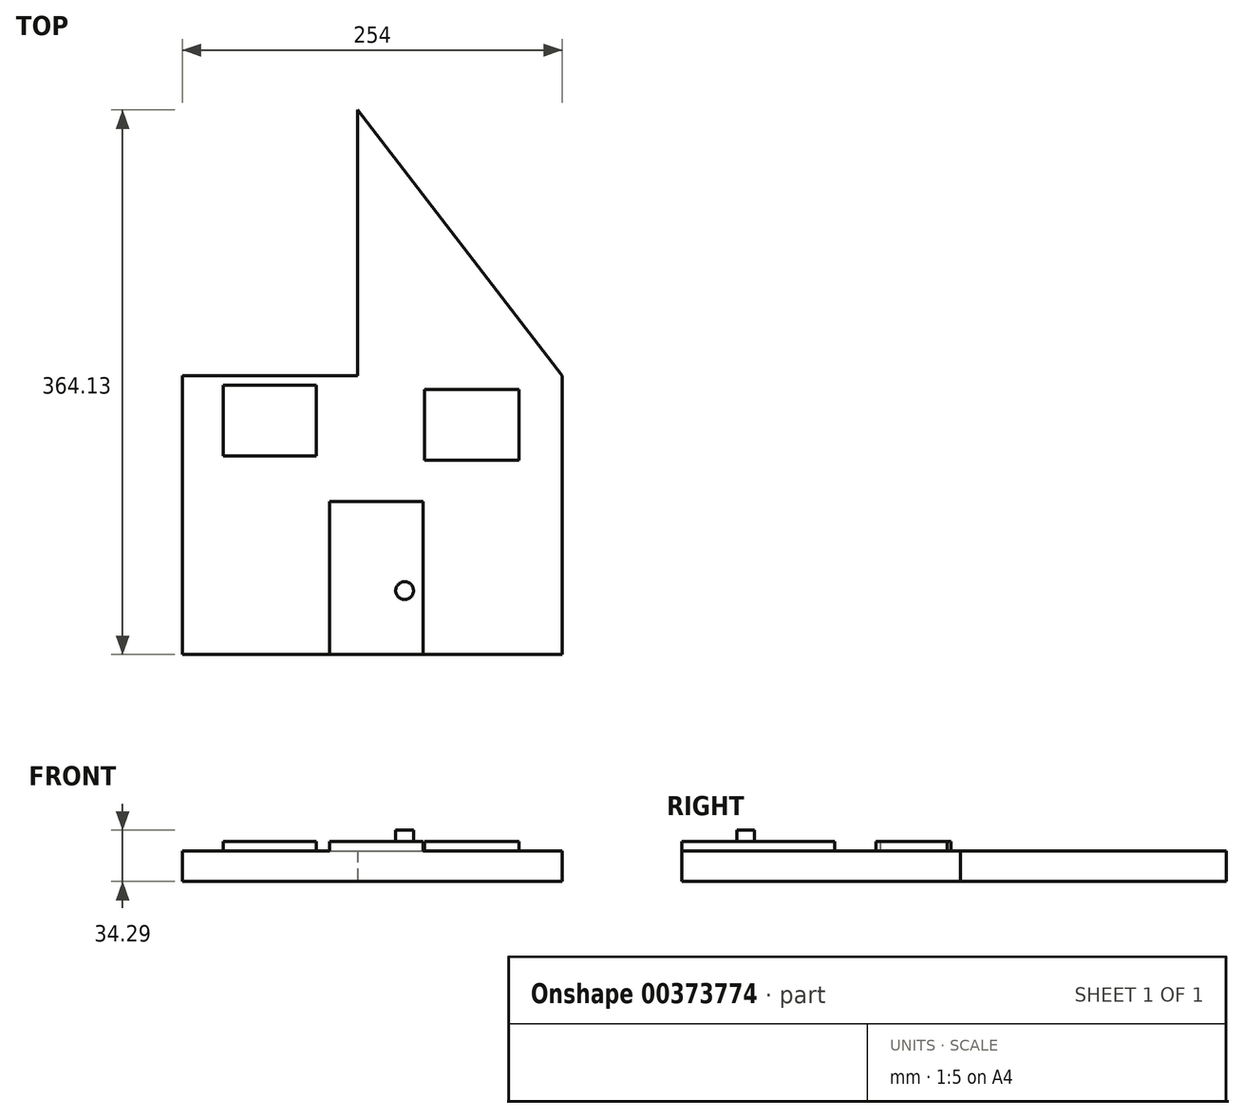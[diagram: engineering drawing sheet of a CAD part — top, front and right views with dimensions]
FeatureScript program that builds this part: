
annotation { "Feature Type Name" : "Feature", "Feature Type Description" : "" }
export const myFeature = defineFeature(function(context is Context, id is Id, definition is map)
    precondition{}
    {
        {
            var Q0;
            Q0=qCreatedBy(makeId("Top.planeOp"),FACE);
            var sketch = newSketch(context, id + "F0", { "sketchPlane" : qUnion([Q0])});
            skLineSegment(sketch, "E0.bottom", {"start": v(-140.68, 104.04) * mm, "end": v(113.32, 104.04) * mm});
            skLineSegment(sketch, "E0.top", {"start": v(-140.68, -82.29) * mm, "end": v(113.32, -82.29) * mm});
            skLineSegment(sketch, "E0.left", {"start": v(-140.68, 104.04) * mm, "end": v(-140.68, -82.29) * mm});
            skLineSegment(sketch, "E0.right", {"start": v(113.32, 104.04) * mm, "end": v(113.32, -82.29) * mm});
            skLineSegment(sketch, "E1.bottom", {"start": v(-66.48, 104.04) * mm, "end": v(-61.53, 104.04) * mm});
            skLineSegment(sketch, "E1.top", {"start": v(-66.48, 104.04) * mm, "end": v(-61.53, 104.04) * mm});
            skLineSegment(sketch, "E1.left", {"start": v(-66.48, 104.04) * mm, "end": v(-66.48, 104.04) * mm});
            skLineSegment(sketch, "E1.right", {"start": v(-61.53, 104.04) * mm, "end": v(-61.53, 104.04) * mm});
            skLineSegment(sketch, "E2", {"start": v(-140.68, 104.04) * mm, "end": v(-23.6, 281.84) * mm});
            skLineSegment(sketch, "E3", {"start": v(-23.6, 281.84) * mm, "end": v(113.32, 104.04) * mm});
            skLineSegment(sketch, "E4", {"start": v(-23.6, 281.84) * mm, "end": v(-23.6, 104.04) * mm});
            skSolve(sketch);
        }
        {
            var Q0;
            Q0=makeQuery(id+"F0.imprint","IMPRINT",FACE,{"disambiguationData":[TD([[makeQuery(id+"F0.imprint","IMPRINT",EDGE,{"derivedFrom":sQuery(id+"F0.wireOp",EDGE,"E0.top")}),1.0]])]});
            var sketch = newSketch(context, id + "F1", { "sketchPlane" : qUnion([Q0])});
            skLineSegment(sketch, "E5.bottom", {"start": v(-39.8, 20.29) * mm, "end": v(12.33, 20.29) * mm});
            skLineSegment(sketch, "E5.top", {"start": v(-39.8, -78.17) * mm, "end": v(12.33, -78.17) * mm});
            skLineSegment(sketch, "E5.left", {"start": v(-39.8, 20.29) * mm, "end": v(-39.8, -78.17) * mm});
            skLineSegment(sketch, "E5.right", {"start": v(12.33, 20.29) * mm, "end": v(12.33, -78.17) * mm});
            skLineSegment(sketch, "E6.bottom", {"start": v(31.64, 88.82) * mm, "end": v(85.7, 88.82) * mm});
            skLineSegment(sketch, "E6.top", {"start": v(31.64, 36.7) * mm, "end": v(85.7, 36.7) * mm});
            skLineSegment(sketch, "E6.left", {"start": v(31.64, 88.82) * mm, "end": v(31.64, 36.7) * mm});
            skLineSegment(sketch, "E6.right", {"start": v(85.7, 88.82) * mm, "end": v(85.7, 36.7) * mm});
            skLineSegment(sketch, "E7.bottom", {"start": v(-119.91, 84) * mm, "end": v(-66.82, 84) * mm});
            skLineSegment(sketch, "E7.top", {"start": v(-119.91, 31.87) * mm, "end": v(-66.82, 31.87) * mm});
            skLineSegment(sketch, "E7.left", {"start": v(-119.91, 84) * mm, "end": v(-119.91, 31.87) * mm});
            skLineSegment(sketch, "E7.right", {"start": v(-66.82, 84) * mm, "end": v(-66.82, 31.87) * mm});
            skSolve(sketch);
        }
        {
            var Q0;
            {var subQ1=sQuery(id+"F0.wireOp",EDGE,"E1.top");Q0=makeQuery(id+"F0.imprint","IMPRINT",FACE,{"disambiguationData":[TD([[makeQuery(id+"F0.imprint","IMPRINT",EDGE,{"derivedFrom":subQ1}),1.0]])]});}
            var Q1;
            {var subQ0=sQuery(id+"F0.wireOp",EDGE,"E3");Q1=makeQuery(id+"F0.imprint","IMPRINT",FACE,{"disambiguationData":[TD([[makeQuery(id+"F0.imprint","IMPRINT",EDGE,{"derivedFrom":subQ0}),-1.0]])]});}
            var Q2;
            Q2=makeQuery(id+"F0.imprint","IMPRINT",FACE,{"disambiguationData":[TD([[makeQuery(id+"F0.imprint","IMPRINT",EDGE,{"derivedFrom":sQuery(id+"F0.wireOp",EDGE,"E0.top")}),1.0]])]});
            extrude(context, id + "F2", {"entities" : qUnion([Q0, Q1, Q2]), "depth" : 5.08 * mm});
        }
        {
            var Q0;
            Q0 = qSketchRegion(id + "F1", true);
            var Q1;
            Q1=makeQuery(id+"F2.opExtrude","CAP_FACE",FACE,{"disambiguationData":[OSD([sQuery(id+"F0.wireOp",EDGE,"E0.top"),sQuery(id+"F0.wireOp",EDGE,"E0.left"),sQuery(id+"F0.wireOp",EDGE,"E0.right"),sQuery(id+"F0.wireOp",EDGE,"E2"),sQuery(id+"F0.wireOp",EDGE,"E3")])],"isStart":false});
            extrude(context, id + "F3", {"entities" : qUnion([Q0, Q1]), "operationType" : NewBodyOperationType.ADD, "depth" : 7.62 * mm});
        }
        {
            var Q0;
            Q0 = qSketchRegion(id + "F1", true);
            var Q1;
            Q1=makeQuery(id+"F3.opExtrude","CAP_FACE",FACE,{"disambiguationData":[OSD([sQuery(id+"F0.wireOp",EDGE,"E0.top"),sQuery(id+"F0.wireOp",EDGE,"E0.left"),sQuery(id+"F0.wireOp",EDGE,"E0.right"),sQuery(id+"F0.wireOp",EDGE,"E2"),sQuery(id+"F0.wireOp",EDGE,"E3")])],"isStart":false});
            extrude(context, id + "F4", {"entities" : qUnion([Q0, Q1]), "operationType" : NewBodyOperationType.ADD, "depth" : 7.62 * mm});
        }
        {
            var Q0;
            Q0=makeQuery(id+"F4.opExtrude","CAP_FACE",FACE,{"disambiguationData":[OSD([sQuery(id+"F0.wireOp",EDGE,"E0.top"),sQuery(id+"F0.wireOp",EDGE,"E0.left"),sQuery(id+"F0.wireOp",EDGE,"E0.right"),sQuery(id+"F0.wireOp",EDGE,"E2"),sQuery(id+"F0.wireOp",EDGE,"E3")])],"isStart":false});
            var sketch = newSketch(context, id + "F5", { "sketchPlane" : qUnion([Q0])});
            skLineSegment(sketch, "E8.bottom", {"start": v(-42.23, 20.04) * mm, "end": v(20.45, 20.04) * mm});
            skLineSegment(sketch, "E8.top", {"start": v(-42.23, -82.29) * mm, "end": v(20.45, -82.29) * mm});
            skLineSegment(sketch, "E8.left", {"start": v(-42.23, 20.04) * mm, "end": v(-42.23, -82.29) * mm});
            skLineSegment(sketch, "E8.right", {"start": v(20.45, 20.04) * mm, "end": v(20.45, -82.29) * mm});
            skSolve(sketch);
        }
        {
            var Q0;
            Q0=makeQuery(id+"F5.imprint","IMPRINT",FACE,{"disambiguationData":[TD([[makeQuery(id+"F5.imprint","IMPRINT",EDGE,{"derivedFrom":sQuery(id+"F5.wireOp",EDGE,"E8.bottom")}),-1.0]])]});
            extrude(context, id + "F6", {"entities" : qUnion([Q0]), "operationType" : NewBodyOperationType.ADD, "depth" : 6.35 * mm});
        }
        {
            var Q0;
            Q0=makeQuery(id+"F6.opExtrude","CAP_FACE",FACE,{"disambiguationData":[OSD([sQuery(id+"F5.wireOp",EDGE,"E8.bottom"),sQuery(id+"F5.wireOp",EDGE,"E8.top"),sQuery(id+"F5.wireOp",EDGE,"E8.left"),sQuery(id+"F5.wireOp",EDGE,"E8.right")])],"isStart":false});
            var sketch = newSketch(context, id + "F7", { "sketchPlane" : qUnion([Q0])});
            skCircle(sketch, "E9", {"center": v(7.91, -39.6) * mm, "radius": 5.95 * mm});
            skSolve(sketch);
        }
        {
            var Q0;
            Q0=makeQuery(id+"F7.imprint","IMPRINT",FACE,{"disambiguationData":[TD([[makeQuery(id+"F7.imprint","IMPRINT",EDGE,{"derivedFrom":sQuery(id+"F7.wireOp",EDGE,"E9")}),1.0]])]});
            extrude(context, id + "F8", {"entities" : qUnion([Q0]), "operationType" : NewBodyOperationType.ADD, "depth" : 7.62 * mm});
        }
        {
            var Q0;
            Q0=makeQuery(id+"F4.opExtrude","CAP_FACE",FACE,{"disambiguationData":[OSD([sQuery(id+"F0.wireOp",EDGE,"E0.top"),sQuery(id+"F0.wireOp",EDGE,"E0.left"),sQuery(id+"F0.wireOp",EDGE,"E0.right"),sQuery(id+"F0.wireOp",EDGE,"E2"),sQuery(id+"F0.wireOp",EDGE,"E3")])],"isStart":false});
            var sketch = newSketch(context, id + "F9", { "sketchPlane" : qUnion([Q0])});
            skLineSegment(sketch, "E10.bottom", {"start": v(-113.26, 97.87) * mm, "end": v(-51.28, 97.87) * mm});
            skLineSegment(sketch, "E10.top", {"start": v(-113.26, 50.51) * mm, "end": v(-51.28, 50.51) * mm});
            skLineSegment(sketch, "E10.left", {"start": v(-113.26, 97.87) * mm, "end": v(-113.26, 50.51) * mm});
            skLineSegment(sketch, "E10.right", {"start": v(-51.28, 97.87) * mm, "end": v(-51.28, 50.51) * mm});
            skLineSegment(sketch, "E11.bottom", {"start": v(21.14, 95.08) * mm, "end": v(84.52, 95.08) * mm});
            skLineSegment(sketch, "E11.top", {"start": v(21.14, 47.73) * mm, "end": v(84.52, 47.73) * mm});
            skLineSegment(sketch, "E11.left", {"start": v(21.14, 95.08) * mm, "end": v(21.14, 47.73) * mm});
            skLineSegment(sketch, "E11.right", {"start": v(84.52, 95.08) * mm, "end": v(84.52, 47.73) * mm});
            skSolve(sketch);
        }
        {
            var Q0;
            Q0=makeQuery(id+"F9.imprint","IMPRINT",FACE,{"disambiguationData":[TD([[makeQuery(id+"F9.imprint","IMPRINT",EDGE,{"derivedFrom":sQuery(id+"F9.wireOp",EDGE,"E10.bottom")}),-1.0]])]});
            var Q1;
            Q1=makeQuery(id+"F9.imprint","IMPRINT",FACE,{"disambiguationData":[TD([[makeQuery(id+"F9.imprint","IMPRINT",EDGE,{"derivedFrom":sQuery(id+"F9.wireOp",EDGE,"E11.bottom")}),-1.0]])]});
            extrude(context, id + "F10", {"entities" : qUnion([Q0, Q1]), "operationType" : NewBodyOperationType.ADD, "depth" : 6.35 * mm});
        }
    });
